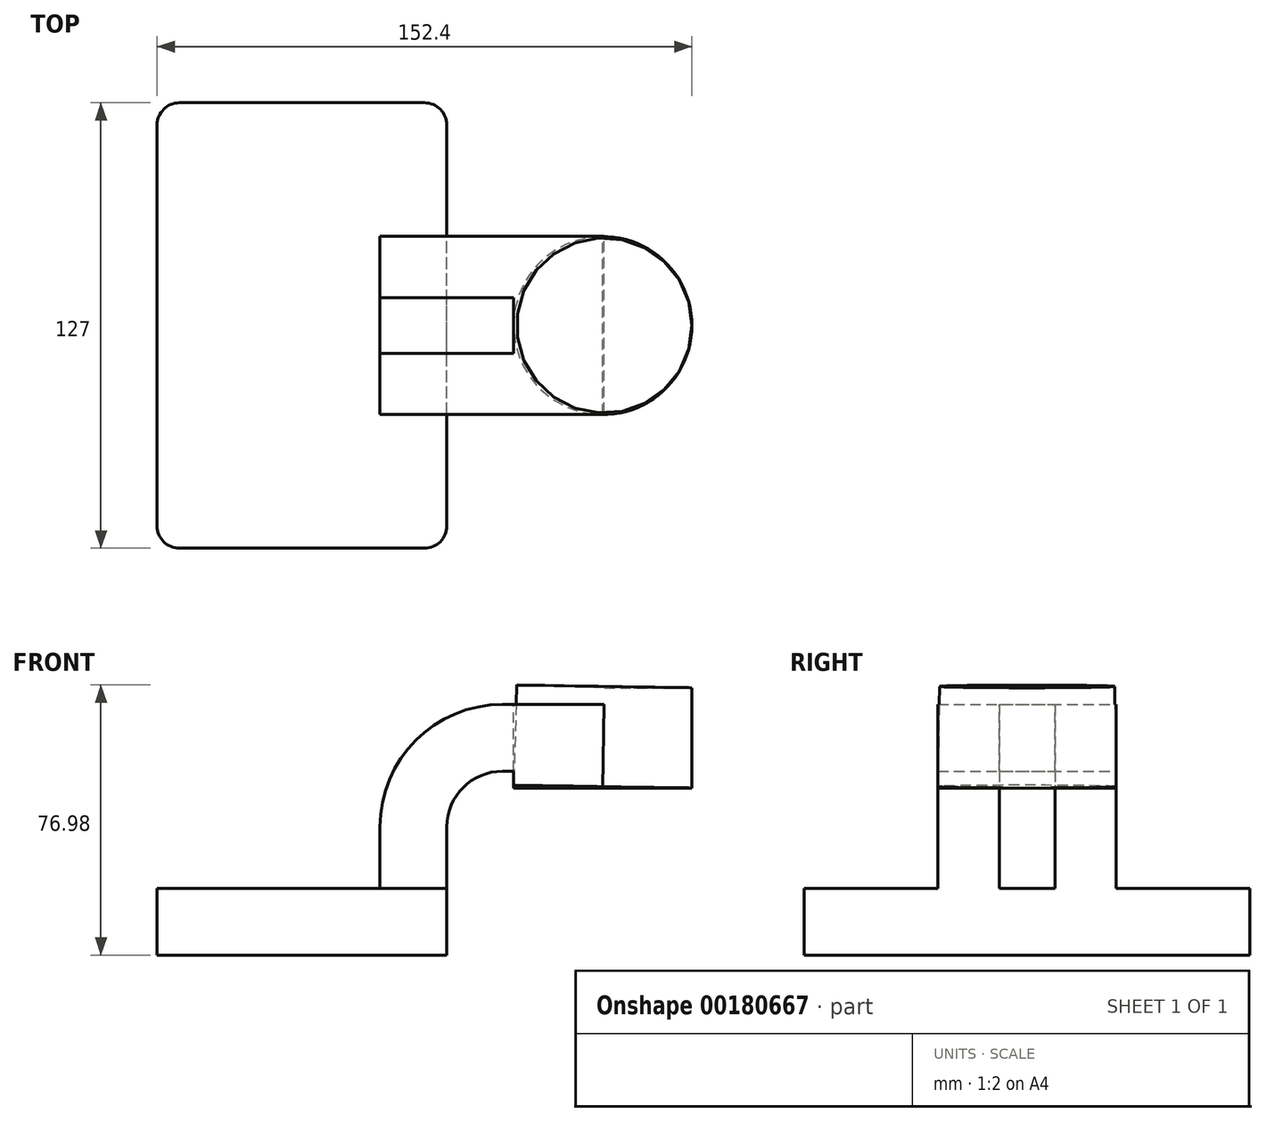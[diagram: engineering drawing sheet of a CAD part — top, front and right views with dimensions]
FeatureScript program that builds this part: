
annotation { "Feature Type Name" : "Feature", "Feature Type Description" : "" }
export const myFeature = defineFeature(function(context is Context, id is Id, definition is map)
    precondition{}
    {
        {
            var Q0;
            Q0=qCreatedBy(makeId("Front.planeOp"),FACE);
            var sketch = newSketch(context, id + "F0", { "sketchPlane" : qUnion([Q0])});
            skLineSegment(sketch, "E0.bottom", {"start": v(-41.28, 9.52) * mm, "end": v(41.28, 9.53) * mm});
            skLineSegment(sketch, "E0.top", {"start": v(-41.28, -9.53) * mm, "end": v(41.28, -9.53) * mm});
            skLineSegment(sketch, "E0.left", {"start": v(-41.28, 9.52) * mm, "end": v(-41.28, -9.53) * mm});
            skLineSegment(sketch, "E0.right", {"start": v(41.28, 9.53) * mm, "end": v(41.28, -9.52) * mm});
            skPoint(sketch, "E0.middle", {"position": v(0, 0) * mm});
            skLineSegment(sketch, "E1.bottom", {"start": v(111.12, 38.1) * mm, "end": v(60.33, 38.1) * mm});
            skLineSegment(sketch, "E1.top", {"start": v(111.12, 66.67) * mm, "end": v(60.33, 66.67) * mm});
            skLineSegment(sketch, "E1.left", {"start": v(111.12, 38.1) * mm, "end": v(111.12, 66.67) * mm});
            skLineSegment(sketch, "E1.right", {"start": v(60.33, 38.1) * mm, "end": v(60.33, 66.67) * mm});
            skPoint(sketch, "E1.middle", {"position": v(85.72, 52.39) * mm});
            skLineSegment(sketch, "E2", {"start": v(41.27, 9.53) * mm, "end": v(41.27, 27) * mm});
            skArc(sketch, "E3", {"start": v(41.27, 27) * mm, "mid": v(45.92, 38.23) * mm, "end": v(57.15, 42.88) * mm});
            skLineSegment(sketch, "E4", {"start": v(57.15, 42.88) * mm, "end": v(85.72, 42.88) * mm});
            skLineSegment(sketch, "E5.0", {"start": v(57.15, 61.93) * mm, "end": v(86.16, 61.93) * mm});
            skArc(sketch, "E5.1", {"start": v(22.23, 27) * mm, "mid": v(32.45, 51.7) * mm, "end": v(57.15, 61.93) * mm});
            skLineSegment(sketch, "E5.2", {"start": v(22.22, 9.53) * mm, "end": v(22.22, 27) * mm});
            skLineSegment(sketch, "E6", {"start": v(86.16, 66.67) * mm, "end": v(85.72, 38.1) * mm});
            skFitSpline(sketch, "E7", {"points": [v(-41.28, 9.52) * mm, v(57.15, 61.93) * mm], "startDerivative": vector(3.26, 102.43) * mm, "endDerivative": vector(135.6, -16.8) * mm});
            skSolve(sketch);
        }
        {
            var Q0;
            Q0=makeQuery(id+"F0.imprint","IMPRINT",FACE,{"disambiguationData":[TD([[makeQuery(id+"F0.imprint","IMPRINT",EDGE,{"derivedFrom":sQuery(id+"F0.wireOp",EDGE,"E0.top")}),1.0]])]});
            extrude(context, id + "F1", {"entities" : qUnion([Q0]), "endBound" : BoundingType.SYMMETRIC, "depth" : 127 * mm});
        }
        {
            var Q0;
            {var subQ2=sQuery(id+"F0.wireOp",EDGE,"E2");Q0=makeQuery(id+"F0.imprint","IMPRINT",FACE,{"disambiguationData":[TD([[makeQuery(id+"F0.imprint","IMPRINT",EDGE,{"derivedFrom":subQ2}),1.0]])]});}
            var Q1;
            {var subQ1=sQuery(id+"F0.wireOp",EDGE,"E1.right");var subQ5=sQuery(id+"F0.wireOp",EDGE,"E1.bottom");var subQ6=makeQuery(id+"F0.imprint","INTERSECT",VERTEX,{"derivedFrom":[subQ5,subQ1]});Q1=makeQuery(id+"F0.imprint","IMPRINT",FACE,{"disambiguationData":[TD([[makeQuery(id+"F0.imprint","IMPRINT",EDGE,{"disambiguationData":[TD([[subQ6,1.0]])],"derivedFrom":subQ5}),-1.0]])]});}
            extrude(context, id + "F2", {"entities" : qUnion([Q0, Q1]), "operationType" : NewBodyOperationType.ADD, "endBound" : BoundingType.SYMMETRIC, "depth" : 50.8 * mm});
        }
        {
            var Q0;
            Q0=makeQuery(id+"F0.imprint","IMPRINT",FACE,{"disambiguationData":[TD([[makeQuery(id+"F0.imprint","IMPRINT",EDGE,{"derivedFrom":sQuery(id+"F0.wireOp",EDGE,"E5.1")}),1.0]])]});
            extrude(context, id + "F3", {"entities" : qUnion([Q0]), "endBound" : BoundingType.SYMMETRIC, "depth" : 15.88 * mm});
        }
        {
            var Q0;
            {var subQ0=sQuery(id+"F0.wireOp",EDGE,"E1.left");Q0=makeQuery(id+"F0.imprint","IMPRINT",FACE,{"disambiguationData":[TD([[makeQuery(id+"F0.imprint","IMPRINT",EDGE,{"derivedFrom":subQ0}),1.0]])]});}
            var Q1;
            Q1=sQuery(id+"F0.wireOp",EDGE,"E6");
            revolve(context, id + "F4", {"entities" : qUnion([Q0]), "axis" : qUnion([Q1]), "revolveType" : RevolveType.FULL});
        }
        {
            var Q0;
            Q0=makeQuery(id+"F1.opExtrude","CAP_EDGE",EDGE,{"disambiguationData":[OSD([sQuery(id+"F0.wireOp",EDGE,"E0.right")])],"isStart":false});
            var Q1;
            Q1=makeQuery(id+"F1.opExtrude","CAP_EDGE",EDGE,{"disambiguationData":[OSD([sQuery(id+"F0.wireOp",EDGE,"E0.left")])],"isStart":false});
            var Q2;
            Q2=makeQuery(id+"F1.opExtrude","CAP_EDGE",EDGE,{"disambiguationData":[OSD([sQuery(id+"F0.wireOp",EDGE,"E0.right")])],"isStart":true});
            var Q3;
            Q3=makeQuery(id+"F1.opExtrude","CAP_EDGE",EDGE,{"disambiguationData":[OSD([sQuery(id+"F0.wireOp",EDGE,"E0.left")])],"isStart":true});
            fillet(context, id + "F5", {"entities" : qUnion([Q0, Q1, Q2, Q3]), "radius" : 6.35 * mm, "tangentPropagation" : true, "allowEdgeOverflow" : false});
        }
    });
